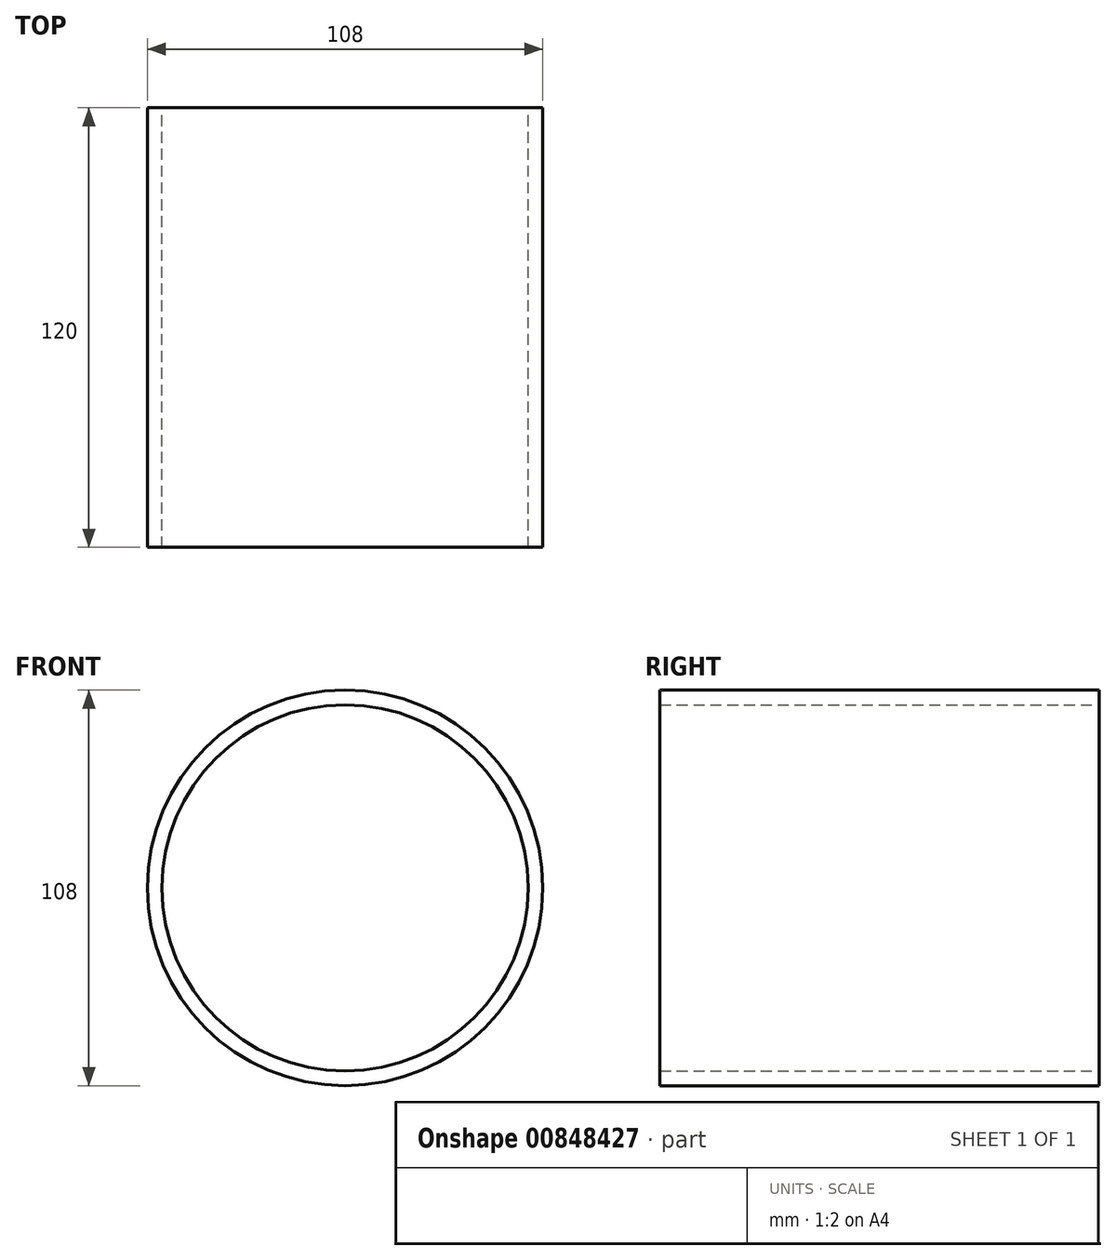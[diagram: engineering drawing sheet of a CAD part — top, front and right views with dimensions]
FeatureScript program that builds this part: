
annotation { "Feature Type Name" : "Feature", "Feature Type Description" : "" }
export const myFeature = defineFeature(function(context is Context, id is Id, definition is map)
    precondition{}
    {
        {
            var Q0;
            Q0=qCreatedBy(makeId("Front.planeOp"),FACE);
            var sketch = newSketch(context, id + "F0", { "sketchPlane" : qUnion([Q0])});
            skCircle(sketch, "E0", {"center": v(0, 0) * mm, "radius": 50 * mm});
            skCircle(sketch, "E1", {"center": v(0, 0) * mm, "radius": 54 * mm});
            skSolve(sketch);
        }
        {
            var Q0;
            Q0=makeQuery(id+"F0.imprint","IMPRINT",FACE,{"disambiguationData":[TD([[makeQuery(id+"F0.imprint","IMPRINT",EDGE,{"derivedFrom":sQuery(id+"F0.wireOp",EDGE,"E0")}),-1.0]])]});
            extrude(context, id + "F1", {"entities" : qUnion([Q0]), "depth" : 120 * mm, "offsetDistance" : 25 * mm});
        }
    });
